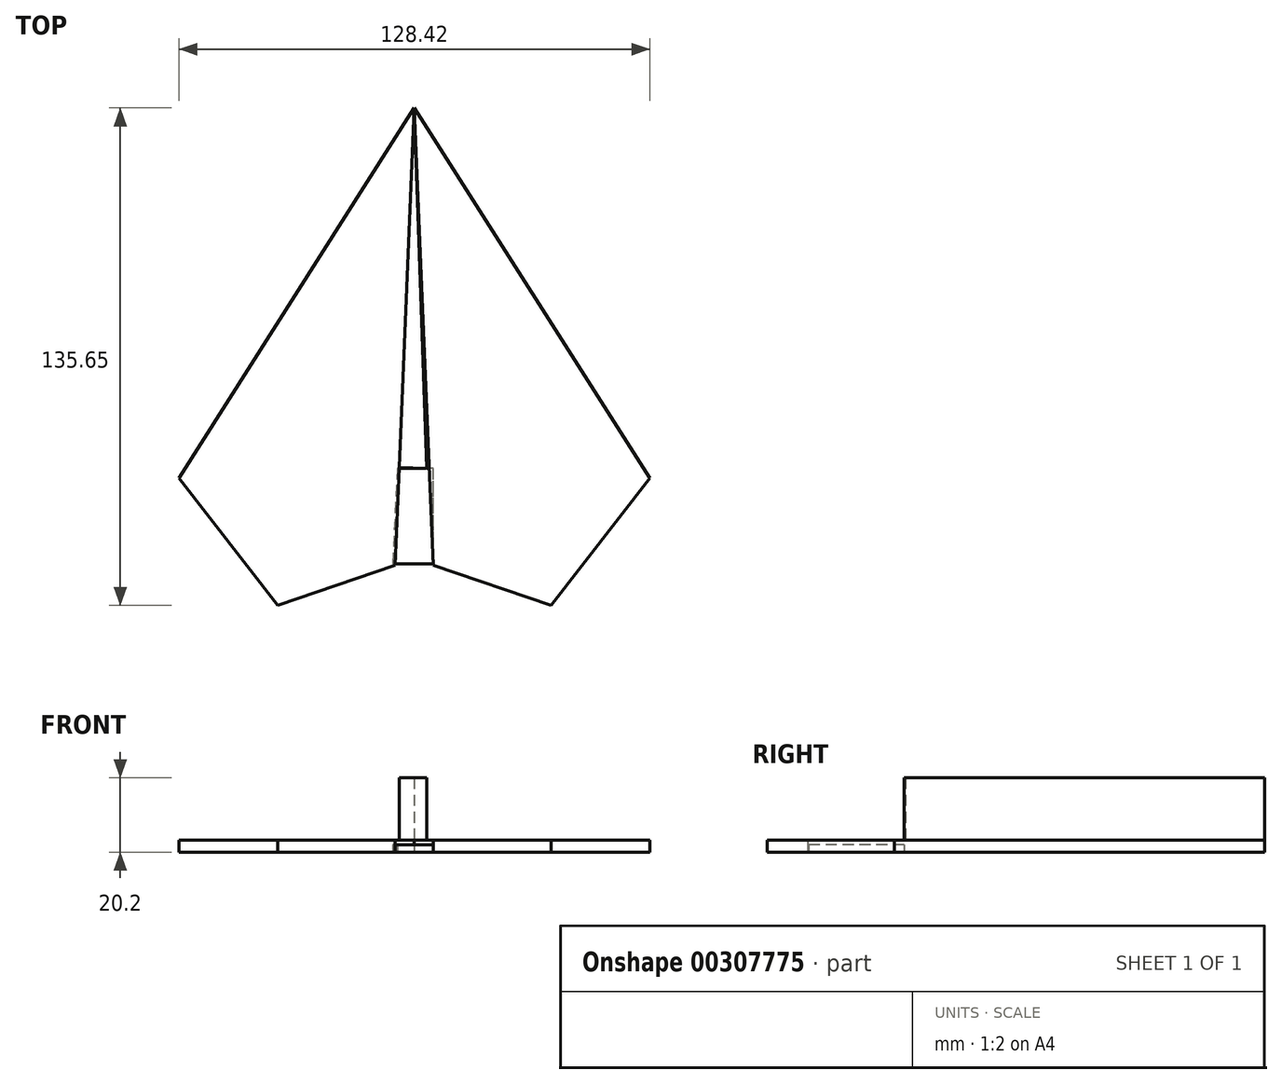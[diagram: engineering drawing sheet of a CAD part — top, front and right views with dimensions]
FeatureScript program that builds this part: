
annotation { "Feature Type Name" : "Feature", "Feature Type Description" : "" }
export const myFeature = defineFeature(function(context is Context, id is Id, definition is map)
    precondition{}
    {
        {
            var Q0;
            Q0=qCreatedBy(makeId("Top.planeOp"),FACE);
            var sketch = newSketch(context, id + "F0", { "sketchPlane" : qUnion([Q0])});
            skLineSegment(sketch, "E0", {"start": v(0, 76.5) * mm, "end": v(-64.21, -24.44) * mm});
            skLineSegment(sketch, "E1", {"start": v(-64.21, -24.44) * mm, "end": v(-37.31, -59.15) * mm});
            skLineSegment(sketch, "E2", {"start": v(0, 76.5) * mm, "end": v(-5.2, -48.16) * mm});
            skLineSegment(sketch, "E3", {"start": v(-37.31, -59.15) * mm, "end": v(-5.2, -48.16) * mm});
            skLineSegment(sketch, "E4", {"start": v(0, -46.42) * mm, "end": v(0, 76.5) * mm});
            skLineSegment(sketch, "E5", {"start": v(-5.2, -48.16) * mm, "end": v(0, -46.42) * mm});
            skLineSegment(sketch, "E6.MirrorCS", {"start": v(5.2, -48.16) * mm, "end": v(0, -46.42) * mm});
            skLineSegment(sketch, "E7.MirrorCS", {"start": v(0, 76.5) * mm, "end": v(5.2, -48.16) * mm});
            skLineSegment(sketch, "E8.MirrorCS", {"start": v(0, 76.5) * mm, "end": v(64.21, -24.44) * mm});
            skLineSegment(sketch, "E9.MirrorCS", {"start": v(64.21, -24.44) * mm, "end": v(37.31, -59.15) * mm});
            skLineSegment(sketch, "E10.MirrorCS", {"start": v(37.31, -59.15) * mm, "end": v(5.2, -48.16) * mm});
            skSolve(sketch);
        }
        {
            var Q0;
            Q0=makeQuery(id+"F0.imprint","IMPRINT",FACE,{"disambiguationData":[TD([[makeQuery(id+"F0.imprint","IMPRINT",EDGE,{"derivedFrom":sQuery(id+"F0.wireOp",EDGE,"E0")}),1.0]])]});
            var Q1;
            Q1=makeQuery(id+"F0.imprint","IMPRINT",FACE,{"disambiguationData":[TD([[makeQuery(id+"F0.imprint","IMPRINT",EDGE,{"derivedFrom":sQuery(id+"F0.wireOp",EDGE,"E7.MirrorCS")}),1.0]])]});
            extrude(context, id + "F1", {"entities" : qUnion([Q0, Q1]), "depth" : 3.2 * mm});
        }
        {
            var Q0;
            Q0=makeQuery(id+"F1.opExtrude","CAP_FACE",FACE,{"disambiguationData":[OSD([sQuery(id+"F0.wireOp",EDGE,"E0"),sQuery(id+"F0.wireOp",EDGE,"E1"),sQuery(id+"F0.wireOp",EDGE,"E2"),sQuery(id+"F0.wireOp",EDGE,"E3")])],"isStart":false});
            var sketch = newSketch(context, id + "F2", { "sketchPlane" : qUnion([Q0])});
            skLineSegment(sketch, "E11", {"start": v(0, 76.5) * mm, "end": v(-4.1, -21.47) * mm});
            skLineSegment(sketch, "E12", {"start": v(-4.1, -21.47) * mm, "end": v(3.43, -21.79) * mm});
            skLineSegment(sketch, "E13", {"start": v(3.43, -21.79) * mm, "end": v(0, 76.5) * mm});
            skLineSegment(sketch, "E14", {"start": v(0, -21.47) * mm, "end": v(0, 76.5) * mm});
            skSolve(sketch);
        }
        {
            var Q0;
            Q0 = qSketchRegion(id + "F2", true);
            extrude(context, id + "F3", {"entities" : qUnion([Q0]), "depth" : 17 * mm});
        }
        {
            var Q0;
            Q0=qCreatedBy(makeId("Top.planeOp"),FACE);
            var sketch = newSketch(context, id + "F4", { "sketchPlane" : qUnion([Q0])});
            skLineSegment(sketch, "E15", {"start": v(-5.9, -47.85) * mm, "end": v(5.14, -47.85) * mm});
            skLineSegment(sketch, "E16", {"start": v(5.14, -47.85) * mm, "end": v(5.14, -21.77) * mm});
            skLineSegment(sketch, "E17", {"start": v(5.14, -21.77) * mm, "end": v(-4.68, -21.77) * mm});
            skLineSegment(sketch, "E18", {"start": v(-4.68, -21.77) * mm, "end": v(-5.9, -47.85) * mm});
            skSolve(sketch);
        }
        {
            var Q0;
            Q0 = qSketchRegion(id + "F4", true);
            extrude(context, id + "F5", {"entities" : qUnion([Q0]), "depth" : 2 * mm});
        }
    });
